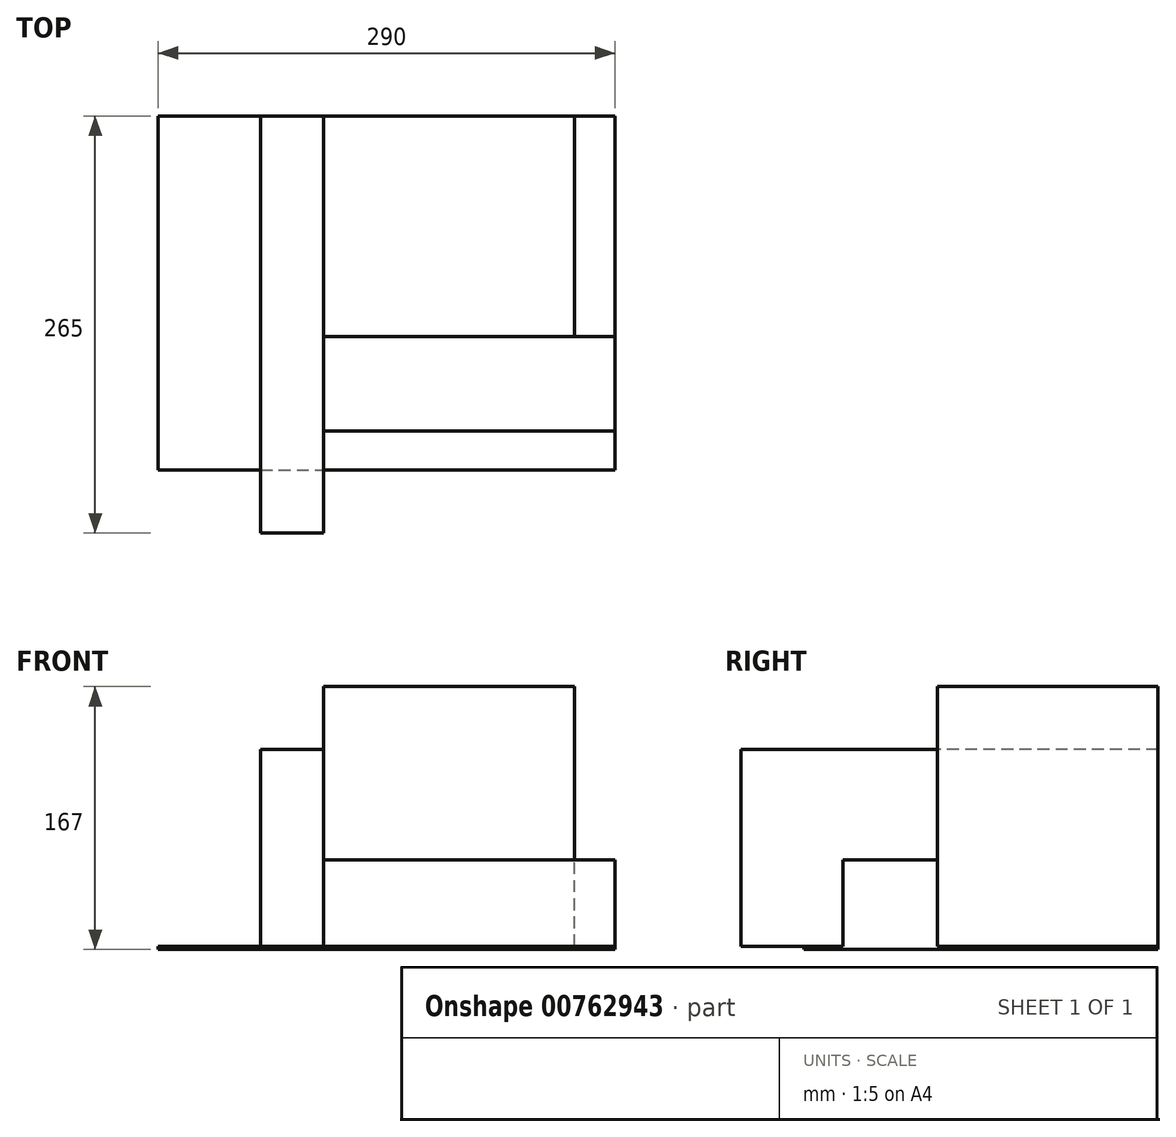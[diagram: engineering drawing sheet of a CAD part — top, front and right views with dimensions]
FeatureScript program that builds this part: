
annotation { "Feature Type Name" : "Feature", "Feature Type Description" : "" }
export const myFeature = defineFeature(function(context is Context, id is Id, definition is map)
    precondition{}
    {
        {
            var Q0;
            Q0=qCreatedBy(makeId("Top.planeOp"),FACE);
            var sketch = newSketch(context, id + "F0", { "sketchPlane" : qUnion([Q0])});
            skLineSegment(sketch, "E0.bottom", {"start": v(-113.22, 160.58) * mm, "end": v(176.78, 160.58) * mm});
            skLineSegment(sketch, "E0.top", {"start": v(-113.22, -64.42) * mm, "end": v(176.78, -64.42) * mm});
            skLineSegment(sketch, "E0.left", {"start": v(-113.22, 160.58) * mm, "end": v(-113.22, -64.42) * mm});
            skLineSegment(sketch, "E0.right", {"start": v(176.78, 160.58) * mm, "end": v(176.78, -64.42) * mm});
            skSolve(sketch);
        }
        {
            var Q0;
            Q0=makeQuery(id+"F0.imprint","IMPRINT",FACE,{"disambiguationData":[TD([[makeQuery(id+"F0.imprint","IMPRINT",EDGE,{"derivedFrom":sQuery(id+"F0.wireOp",EDGE,"E0.bottom")}),-1.0]])]});
            extrude(context, id + "F1", {"entities" : qUnion([Q0]), "depth" : 2 * mm, "offsetDistance" : 25 * mm});
        }
        {
            var Q0;
            Q0=makeQuery(id+"F1.opExtrude","CAP_FACE",FACE,{"disambiguationData":[OSD([sQuery(id+"F0.wireOp",EDGE,"E0.bottom"),sQuery(id+"F0.wireOp",EDGE,"E0.top"),sQuery(id+"F0.wireOp",EDGE,"E0.left"),sQuery(id+"F0.wireOp",EDGE,"E0.right")])],"isStart":false});
            var sketch = newSketch(context, id + "F2", { "sketchPlane" : qUnion([Q0])});
            skLineSegment(sketch, "E1.bottom", {"start": v(-48.22, 160.58) * mm, "end": v(-8.22, 160.58) * mm});
            skLineSegment(sketch, "E1.top", {"start": v(-48.22, -104.42) * mm, "end": v(-8.22, -104.42) * mm});
            skLineSegment(sketch, "E1.left", {"start": v(-48.22, 160.58) * mm, "end": v(-48.22, -104.42) * mm});
            skLineSegment(sketch, "E1.right", {"start": v(-8.22, 160.58) * mm, "end": v(-8.22, -104.42) * mm});
            skSolve(sketch);
        }
        {
            var Q0;
            {var subQ0=sQuery(id+"F2.wireOp",EDGE,"E1.bottom");Q0=makeQuery(id+"F2.imprint","IMPRINT",FACE,{"disambiguationData":[TD([[makeQuery(id+"F2.imprint","IMPRINT",EDGE,{"derivedFrom":subQ0}),-1.0]])]});}
            var Q1;
            {var subQ0=sQuery(id+"F2.wireOp",EDGE,"E1.top");Q1=makeQuery(id+"F2.imprint","IMPRINT",FACE,{"disambiguationData":[TD([[makeQuery(id+"F2.imprint","IMPRINT",EDGE,{"derivedFrom":subQ0}),1.0]])]});}
            extrude(context, id + "F3", {"entities" : qUnion([Q0, Q1]), "operationType" : NewBodyOperationType.ADD, "depth" : 125 * mm, "offsetDistance" : 25 * mm});
        }
        {
            var Q0;
            {var subQ1=sQuery(id+"F0.wireOp",EDGE,"E0.top");var subQ2=sQuery(id+"F0.wireOp",EDGE,"E0.right");var subQ3=sQuery(id+"F0.wireOp",EDGE,"E0.bottom");Q0=makeQuery(id+"F3.boolean.opBoolean","SPLIT",FACE,{"disambiguationData":[TD([makeQuery(id+"F1.opExtrude","SWEPT_FACE",FACE,{"disambiguationData":[OSD([subQ2])]})])],"derivedFrom":makeQuery(id+"F1.opExtrude","CAP_FACE",FACE,{"disambiguationData":[OSD([subQ3,subQ1,sQuery(id+"F0.wireOp",EDGE,"E0.left"),subQ2])],"isStart":false})});}
            var sketch = newSketch(context, id + "F4", { "sketchPlane" : qUnion([Q0])});
            skLineSegment(sketch, "E2.bottom", {"start": v(176.78, 160.58) * mm, "end": v(-8.22, 160.58) * mm});
            skLineSegment(sketch, "E2.top", {"start": v(176.78, 20.58) * mm, "end": v(-8.22, 20.58) * mm});
            skLineSegment(sketch, "E2.left", {"start": v(176.78, 160.58) * mm, "end": v(176.78, 20.58) * mm});
            skLineSegment(sketch, "E2.right", {"start": v(-8.22, 160.58) * mm, "end": v(-8.22, 20.58) * mm});
            skSolve(sketch);
        }
        {
            var Q0;
            Q0=makeQuery(id+"F4.imprint","IMPRINT",FACE,{"disambiguationData":[TD([[makeQuery(id+"F4.imprint","IMPRINT",EDGE,{"derivedFrom":sQuery(id+"F4.wireOp",EDGE,"E2.bottom")}),-1.0]])]});
            extrude(context, id + "F5", {"entities" : qUnion([Q0]), "operationType" : NewBodyOperationType.ADD, "depth" : 165 * mm, "offsetDistance" : 25 * mm});
        }
        {
            var Q0;
            {var subQ1=sQuery(id+"F0.wireOp",EDGE,"E0.top");var subQ2=sQuery(id+"F0.wireOp",EDGE,"E0.right");var subQ3=sQuery(id+"F0.wireOp",EDGE,"E0.bottom");Q0=makeQuery(id+"F3.boolean.opBoolean","SPLIT",FACE,{"disambiguationData":[TD([makeQuery(id+"F1.opExtrude","SWEPT_FACE",FACE,{"disambiguationData":[OSD([subQ2])]})])],"derivedFrom":makeQuery(id+"F1.opExtrude","CAP_FACE",FACE,{"disambiguationData":[OSD([subQ3,subQ1,sQuery(id+"F0.wireOp",EDGE,"E0.left"),subQ2])],"isStart":false})});}
            var sketch = newSketch(context, id + "F6", { "sketchPlane" : qUnion([Q0])});
            skLineSegment(sketch, "E3.bottom", {"start": v(-8.22, 20.58) * mm, "end": v(176.78, 20.58) * mm});
            skLineSegment(sketch, "E3.top", {"start": v(-8.22, -39.42) * mm, "end": v(176.78, -39.42) * mm});
            skLineSegment(sketch, "E3.left", {"start": v(-8.22, 20.58) * mm, "end": v(-8.22, -39.42) * mm});
            skLineSegment(sketch, "E3.right", {"start": v(176.78, 20.58) * mm, "end": v(176.78, -39.42) * mm});
            skSolve(sketch);
        }
        {
            var Q0;
            Q0=makeQuery(id+"F6.imprint","IMPRINT",FACE,{"disambiguationData":[TD([[makeQuery(id+"F6.imprint","IMPRINT",EDGE,{"derivedFrom":sQuery(id+"F6.wireOp",EDGE,"E3.bottom")}),1.0]])]});
            extrude(context, id + "F7", {"entities" : qUnion([Q0]), "operationType" : NewBodyOperationType.ADD, "depth" : 55 * mm, "offsetDistance" : 25 * mm});
        }
        {
            var Q0;
            Q0=makeQuery(id+"F5.opExtrude","CAP_FACE",FACE,{"disambiguationData":[OSD([sQuery(id+"F4.wireOp",EDGE,"E2.bottom"),sQuery(id+"F4.wireOp",EDGE,"E2.top"),sQuery(id+"F4.wireOp",EDGE,"E2.left"),sQuery(id+"F4.wireOp",EDGE,"E2.right")])],"isStart":false});
            var sketch = newSketch(context, id + "F8", { "sketchPlane" : qUnion([Q0])});
            skLineSegment(sketch, "E4.bottom", {"start": v(176.78, 160.58) * mm, "end": v(150.98, 160.58) * mm});
            skLineSegment(sketch, "E4.top", {"start": v(176.78, 20.58) * mm, "end": v(150.98, 20.58) * mm});
            skLineSegment(sketch, "E4.left", {"start": v(176.78, 160.58) * mm, "end": v(176.78, 20.58) * mm});
            skLineSegment(sketch, "E5", {"start": v(150.98, 20.58) * mm, "end": v(150.98, 160.58) * mm});
            skSolve(sketch);
        }
        {
            var Q0;
            Q0=makeQuery(id+"F8.imprint","IMPRINT",FACE,{"disambiguationData":[TD([[makeQuery(id+"F8.imprint","IMPRINT",EDGE,{"derivedFrom":sQuery(id+"F8.wireOp",EDGE,"E4.bottom")}),-1.0]])]});
            extrude(context, id + "F9", {"entities" : qUnion([Q0]), "operationType" : NewBodyOperationType.REMOVE, "oppositeDirection" : true, "depth" : 165 * mm, "offsetDistance" : 25 * mm});
        }
    });
